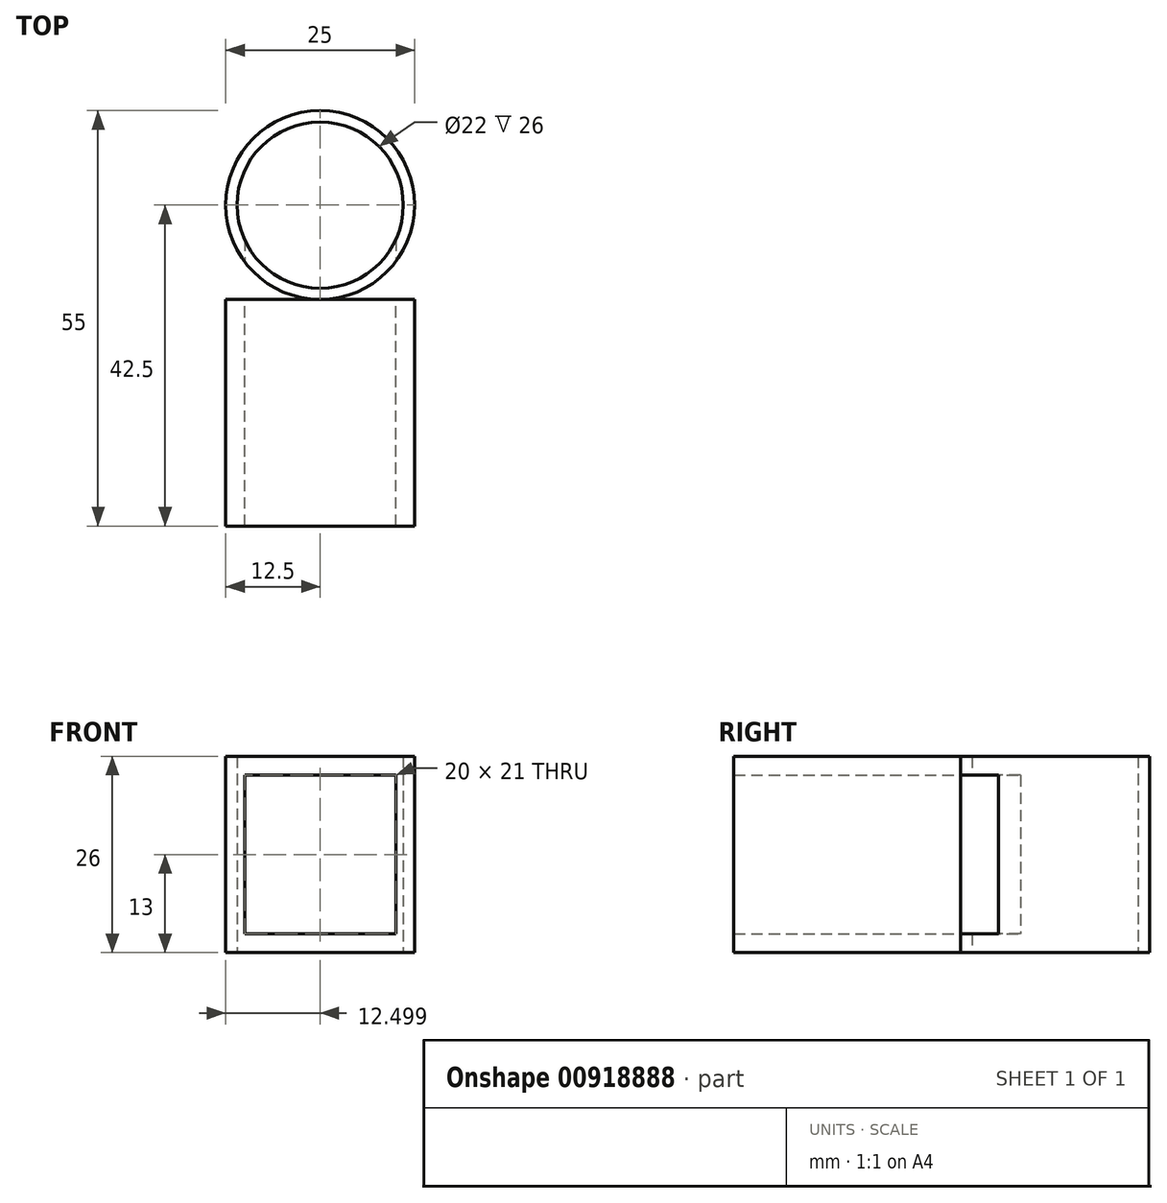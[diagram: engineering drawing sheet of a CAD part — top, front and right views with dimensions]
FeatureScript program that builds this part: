
annotation { "Feature Type Name" : "Feature", "Feature Type Description" : "" }
export const myFeature = defineFeature(function(context is Context, id is Id, definition is map)
    precondition{}
    {
        {
            var Q0;
            Q0=qCreatedBy(makeId("Top.planeOp"),FACE);
            var sketch = newSketch(context, id + "F0", { "sketchPlane" : qUnion([Q0])});
            skCircle(sketch, "E0", {"center": v(0, 0) * mm, "radius": 12.5 * mm});
            skCircle(sketch, "E1", {"center": v(0, 0) * mm, "radius": 11 * mm});
            skLineSegment(sketch, "E2", {"start": v(19.93, 0) * mm, "end": v(-20.38, 0) * mm});
            skLineSegment(sketch, "E3", {"start": v(0, -20.54) * mm, "end": v(0, 19.29) * mm});
            skSolve(sketch);
        }
        {
            var Q0;
            Q0=makeQuery(id+"F0.imprint","IMPRINT",FACE,{"disambiguationData":[TD([[makeQuery(id+"F0.imprint","IMPRINT",EDGE,{"derivedFrom":sQuery(id+"F0.wireOp",EDGE,"E0")}),1.0]])]});
            extrude(context, id + "F1", {"entities" : qUnion([Q0]), "depth" : 26 * mm, "offsetDistance" : 25 * mm});
        }
        {
            var Q0;
            Q0=qCreatedBy(makeId("Front.planeOp"),FACE);
            cPlane(context, id + "F2", {"entities" : qUnion([Q0]), "cplaneType" : CPlaneType.OFFSET, "offset" : 12.5 * mm, "width" : 150 * mm, "height" : 150 * mm});
        }
        {
            var Q0;
            Q0=qCreatedBy(id+"F2.planeOp",FACE);
            var sketch = newSketch(context, id + "F3", { "sketchPlane" : qUnion([Q0])});
            skLineSegment(sketch, "E4.bottom", {"start": v(-12.5, 0) * mm, "end": v(12.5, 0) * mm});
            skLineSegment(sketch, "E4.top", {"start": v(-12.5, 26) * mm, "end": v(12.5, 26) * mm});
            skLineSegment(sketch, "E4.left", {"start": v(-12.5, 0) * mm, "end": v(-12.5, 26) * mm});
            skLineSegment(sketch, "E4.right", {"start": v(12.5, 0) * mm, "end": v(12.5, 26) * mm});
            skSolve(sketch);
        }
        {
            var Q0;
            Q0=makeQuery(id+"F3.imprint","IMPRINT",FACE,{"disambiguationData":[TD([[makeQuery(id+"F3.imprint","IMPRINT",EDGE,{"derivedFrom":sQuery(id+"F3.wireOp",EDGE,"E4.bottom")}),1.0]])]});
            var Q1;
            Q1 = qSketchRegion(id + "F3", true);
            extrude(context, id + "F4", {"entities" : qUnion([Q0, Q1]), "operationType" : NewBodyOperationType.ADD, "depth" : 30 * mm, "offsetDistance" : 25 * mm});
        }
        {
            var Q0;
            Q0=makeQuery(id+"F4.opExtrude","CAP_FACE",FACE,{"disambiguationData":[OSD([sQuery(id+"F3.wireOp",EDGE,"E4.bottom"),sQuery(id+"F3.wireOp",EDGE,"E4.top"),sQuery(id+"F3.wireOp",EDGE,"E4.left"),sQuery(id+"F3.wireOp",EDGE,"E4.right")])],"isStart":false});
            shell(context, id + "F5", {"entities" : qUnion([Q0]), "thickness" : 2.5 * mm});
        }
        {
            var Q0;
            Q0=makeQuery(id+"F5.opShell","OFFSET_FACE",FACE,{"disambiguationData":[OSD([sQuery(id+"F3.wireOp",EDGE,"E4.bottom"),sQuery(id+"F3.wireOp",EDGE,"E4.top"),sQuery(id+"F3.wireOp",EDGE,"E4.left"),sQuery(id+"F3.wireOp",EDGE,"E4.right")])]});
            extrude(context, id + "F6", {"entities" : qUnion([Q0]), "operationType" : NewBodyOperationType.REMOVE, "oppositeDirection" : true, "depth" : 15 * mm, "offsetDistance" : 25 * mm});
        }
    });
